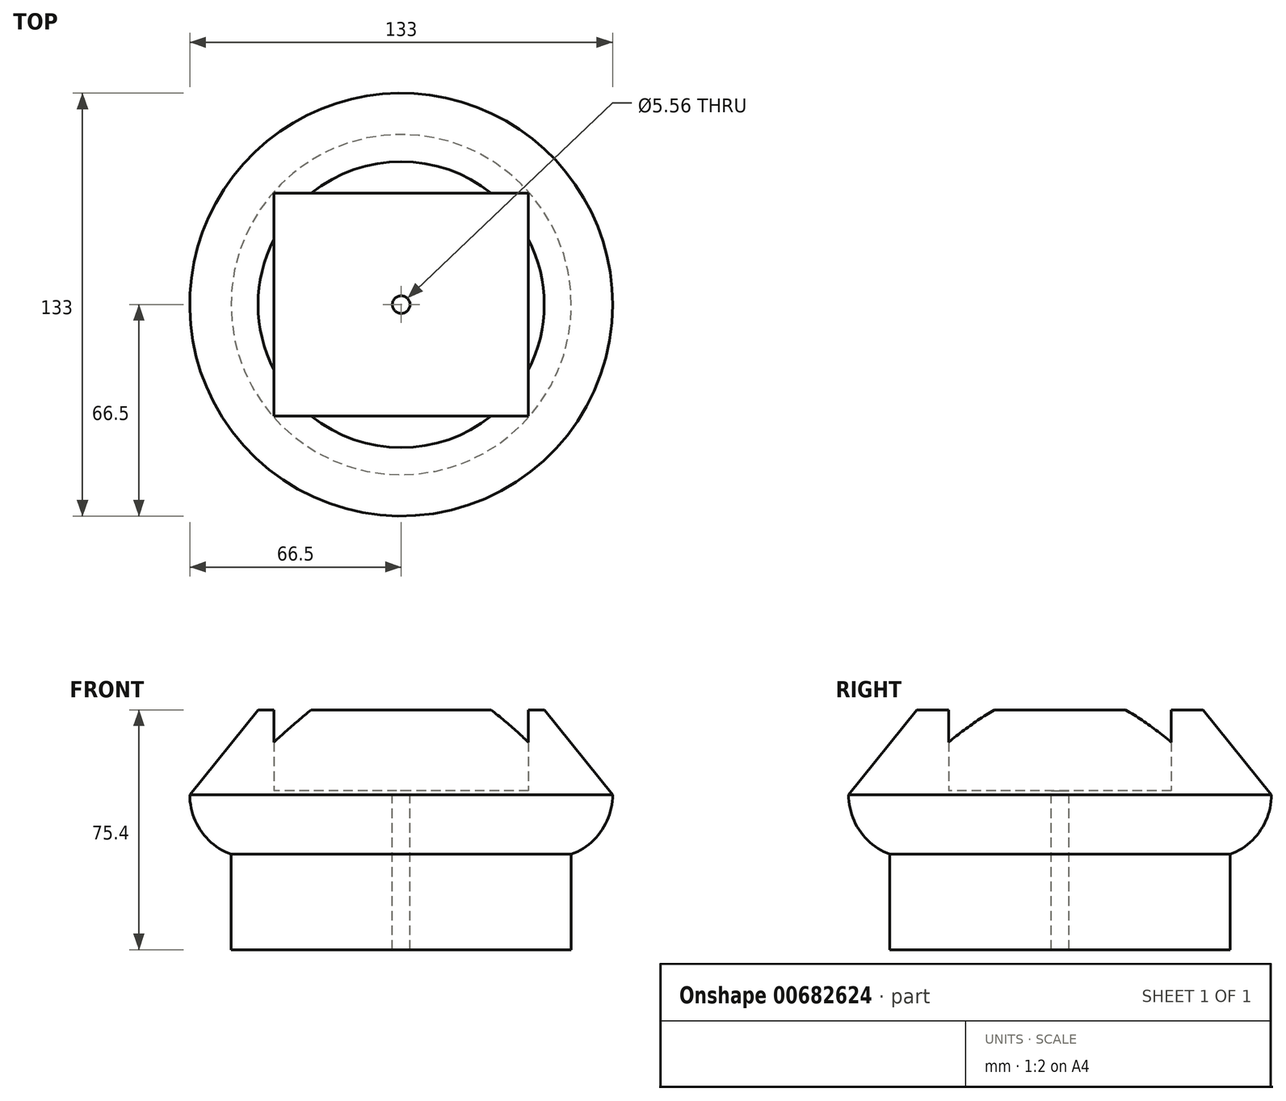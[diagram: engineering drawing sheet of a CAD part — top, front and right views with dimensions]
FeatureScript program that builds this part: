
annotation { "Feature Type Name" : "Feature", "Feature Type Description" : "" }
export const myFeature = defineFeature(function(context is Context, id is Id, definition is map)
    precondition{}
    {
        {
            var Q0;
            Q0=qCreatedBy(makeId("Top.planeOp"),FACE);
            var sketch = newSketch(context, id + "F0", { "sketchPlane" : qUnion([Q0])});
            skCircle(sketch, "E0", {"center": v(0, 0) * mm, "radius": 53.5 * mm});
            skSolve(sketch);
        }
        {
            var Q0;
            Q0=makeQuery(id+"F0.imprint","IMPRINT",FACE,{"disambiguationData":[TD([[makeQuery(id+"F0.imprint","IMPRINT",EDGE,{"derivedFrom":sQuery(id+"F0.wireOp",EDGE,"E0")}),1.0]])]});
            extrude(context, id + "F1", {"entities" : qUnion([Q0]), "depth" : 30 * mm, "offsetDistance" : 25 * mm});
        }
        {
            var Q0;
            Q0=makeQuery(id+"F1.opExtrude","CAP_FACE",FACE,{"disambiguationData":[OSD([sQuery(id+"F0.wireOp",EDGE,"E0")])],"isStart":false});
            var sketch = newSketch(context, id + "F2", { "sketchPlane" : qUnion([Q0])});
            skPoint(sketch, "E1", {"position": v(0, 0) * mm});
            skSolve(sketch);
        }
        {
            var Q0;
            Q0=sQuery(id+"F2.wireOp",VERTEX,"E1");
            var Q1;
            Q1=makeQuery(id+"F1.opExtrude","SWEPT_BODY",BODY,{"disambiguationData":[OSD([sQuery(id+"F0.wireOp",EDGE,"E0")])]});
            hole(context, id + "F3", {"style" : HoleStyle.SIMPLE, "endStyle" : HoleEndStyle.BLIND, "standardTappedOrClearance" : lookupTablePath({ "standard" : "ANSI", "engagement" : "50%", "pitch" : "20 tpi", "size" : "1/4", "type" : "Tapped" }), "standardBlindInLast" : lookupTablePath({ "standard" : "ANSI", "engagement" : "50%", "pitch" : "20 tpi", "size" : "1/4", "type" : "Tapped" }), "holeDiameter" : 5.56 * mm, "majorDiameter" : 6.35 * mm, "showTappedDepth" : true, "holeDepth" : 30.48 * mm, "isTappedThrough" : true, "tappedDepth" : 25.4 * mm, "tapClearance" : 4, "locations" : qUnion([Q0]), "scope" : qUnion([Q1])});
        }
        {
            var Q0;
            Q0=makeQuery(id+"F1.opExtrude","CAP_FACE",FACE,{"disambiguationData":[OSD([sQuery(id+"F0.wireOp",EDGE,"E0")])],"isStart":false});
            var sketch = newSketch(context, id + "F4", { "sketchPlane" : qUnion([Q0])});
            skCircle(sketch, "E2", {"center": v(0, 0) * mm, "radius": 66.5 * mm});
            skSolve(sketch);
        }
        {
            var Q0;
            Q0=makeQuery(id+"F4.imprint","IMPRINT",FACE,{"disambiguationData":[TD([[makeQuery(id+"F4.imprint","IMPRINT",EDGE,{"derivedFrom":sQuery(id+"F4.wireOp",EDGE,"E2")}),1.0]])]});
            var Q1;
            Q1=makeQuery(id+"F4.imprint","IMPRINT",FACE,{"disambiguationData":[TD([[makeQuery(id+"F4.imprint","IMPRINT",EDGE,{"derivedFrom":makeQuery(id+"F1.opExtrude","CAP_EDGE",EDGE,{"disambiguationData":[OSD([sQuery(id+"F0.wireOp",EDGE,"E0")])],"isStart":false})}),1.0]])]});
            extrude(context, id + "F5", {"entities" : qUnion([Q0, Q1]), "operationType" : NewBodyOperationType.ADD, "depth" : 20 * mm, "offsetDistance" : 25 * mm});
        }
        {
            var Q0;
            Q0=makeQuery(id+"F5.opExtrude","CAP_FACE",FACE,{"disambiguationData":[OSD([sQuery(id+"F3.hole-0.sketch.wireOp",EDGE,"core_line_2"),sQuery(id+"F3.hole-0.sketch.wireOp",EDGE,"core_line_3"),sQuery(id+"F4.wireOp",EDGE,"E2")])],"isStart":false});
            var sketch = newSketch(context, id + "F6", { "sketchPlane" : qUnion([Q0])});
            skCircle(sketch, "E3", {"center": v(0, 0) * mm, "radius": 55 * mm});
            skCircle(sketch, "E4.0.0", {"center": v(0, 0) * mm, "radius": 66.5 * mm});
            skSolve(sketch);
        }
        {
            var Q0;
            Q0=makeQuery(id+"F6.imprint","IMPRINT",FACE,{"disambiguationData":[TD([[makeQuery(id+"F6.imprint","IMPRINT",EDGE,{"derivedFrom":sQuery(id+"F6.wireOp",EDGE,"E3")}),-1.0]])]});
            extrude(context, id + "F7", {"entities" : qUnion([Q0]), "operationType" : NewBodyOperationType.ADD, "depth" : 25.4 * mm, "offsetDistance" : 25 * mm});
        }
        {
            var Q0;
            Q0=makeQuery(id+"F5.opExtrude","CAP_EDGE",EDGE,{"disambiguationData":[OSD([sQuery(id+"F4.wireOp",EDGE,"E2")])],"isStart":true});
            fillet(context, id + "F8", {"entities" : qUnion([Q0]), "radius" : 20 * mm, "tangentPropagation" : true, "allowEdgeOverflow" : false});
        }
        {
            var Q0;
            Q0=makeQuery(id+"F5.opExtrude","CAP_FACE",FACE,{"disambiguationData":[OSD([sQuery(id+"F3.hole-0.sketch.wireOp",EDGE,"core_line_2"),sQuery(id+"F3.hole-0.sketch.wireOp",EDGE,"core_line_3"),sQuery(id+"F4.wireOp",EDGE,"E2")])],"isStart":false});
            var sketch = newSketch(context, id + "F9", { "sketchPlane" : qUnion([Q0])});
            skLineSegment(sketch, "E5.bottom", {"start": v(40, 35) * mm, "end": v(-40, 35) * mm});
            skLineSegment(sketch, "E5.top", {"start": v(40, -35) * mm, "end": v(-40, -35) * mm});
            skLineSegment(sketch, "E5.left", {"start": v(40, 35) * mm, "end": v(40, -35) * mm});
            skLineSegment(sketch, "E5.right", {"start": v(-40, 35) * mm, "end": v(-40, -35) * mm});
            skPoint(sketch, "E5.middle", {"position": v(0, 0) * mm});
            skSolve(sketch);
        }
        {
            var Q0;
            Q0=makeQuery(id+"F9.imprint","IMPRINT",FACE,{"disambiguationData":[TD([[makeQuery(id+"F9.imprint","IMPRINT",EDGE,{"derivedFrom":sQuery(id+"F9.wireOp",EDGE,"E5.bottom")}),-1.0]])]});
            extrude(context, id + "F10", {"entities" : qUnion([Q0]), "operationType" : NewBodyOperationType.ADD, "depth" : 25.4 * mm, "offsetDistance" : 25 * mm});
        }
        {
            var Q0;
            Q0=qCreatedBy(makeId("Right.planeOp"),FACE);
            var sketch = newSketch(context, id + "F11", { "sketchPlane" : qUnion([Q0])});
            skLineSegment(sketch, "E6.0.0", {"start": v(-35, 50) * mm, "end": v(35, 50) * mm});
            skLineSegment(sketch, "E6.0.1", {"start": v(35, 50) * mm, "end": v(35, 75.4) * mm});
            skLineSegment(sketch, "E6.0.2", {"start": v(35, 75.4) * mm, "end": v(-35, 75.4) * mm});
            skLineSegment(sketch, "E6.0.3", {"start": v(-35, 75.4) * mm, "end": v(-35, 50) * mm});
            skLineSegment(sketch, "E7", {"start": v(-66.5, 48.73) * mm, "end": v(-66.5, 75.4) * mm});
            skLineSegment(sketch, "E8", {"start": v(66.5, 75.4) * mm, "end": v(66.5, 48.73) * mm});
            skLineSegment(sketch, "E9", {"start": v(66.5, 48.73) * mm, "end": v(45, 75.4) * mm});
            skLineSegment(sketch, "E10", {"start": v(45, 75.4) * mm, "end": v(66.5, 75.4) * mm});
            skLineSegment(sketch, "E11", {"start": v(0, 50) * mm, "end": v(0, 75.4) * mm});
            skSolve(sketch);
        }
        {
            var Q0;
            Q0=makeQuery(id+"F11.imprint","IMPRINT",FACE,{"disambiguationData":[TD([[makeQuery(id+"F11.imprint","IMPRINT",EDGE,{"derivedFrom":sQuery(id+"F11.wireOp",EDGE,"E9")}),-1.0]])]});
            var Q1;
            Q1=sQuery(id+"F11.wireOp",EDGE,"E11");
            revolve(context, id + "F12", {"operationType" : NewBodyOperationType.REMOVE, "surfaceOperationType" : NewSurfaceOperationType.NEW, "entities" : qUnion([Q0]), "axis" : qUnion([Q1]), "revolveType" : RevolveType.FULL, "oppositeDirection" : true});
        }
    });
